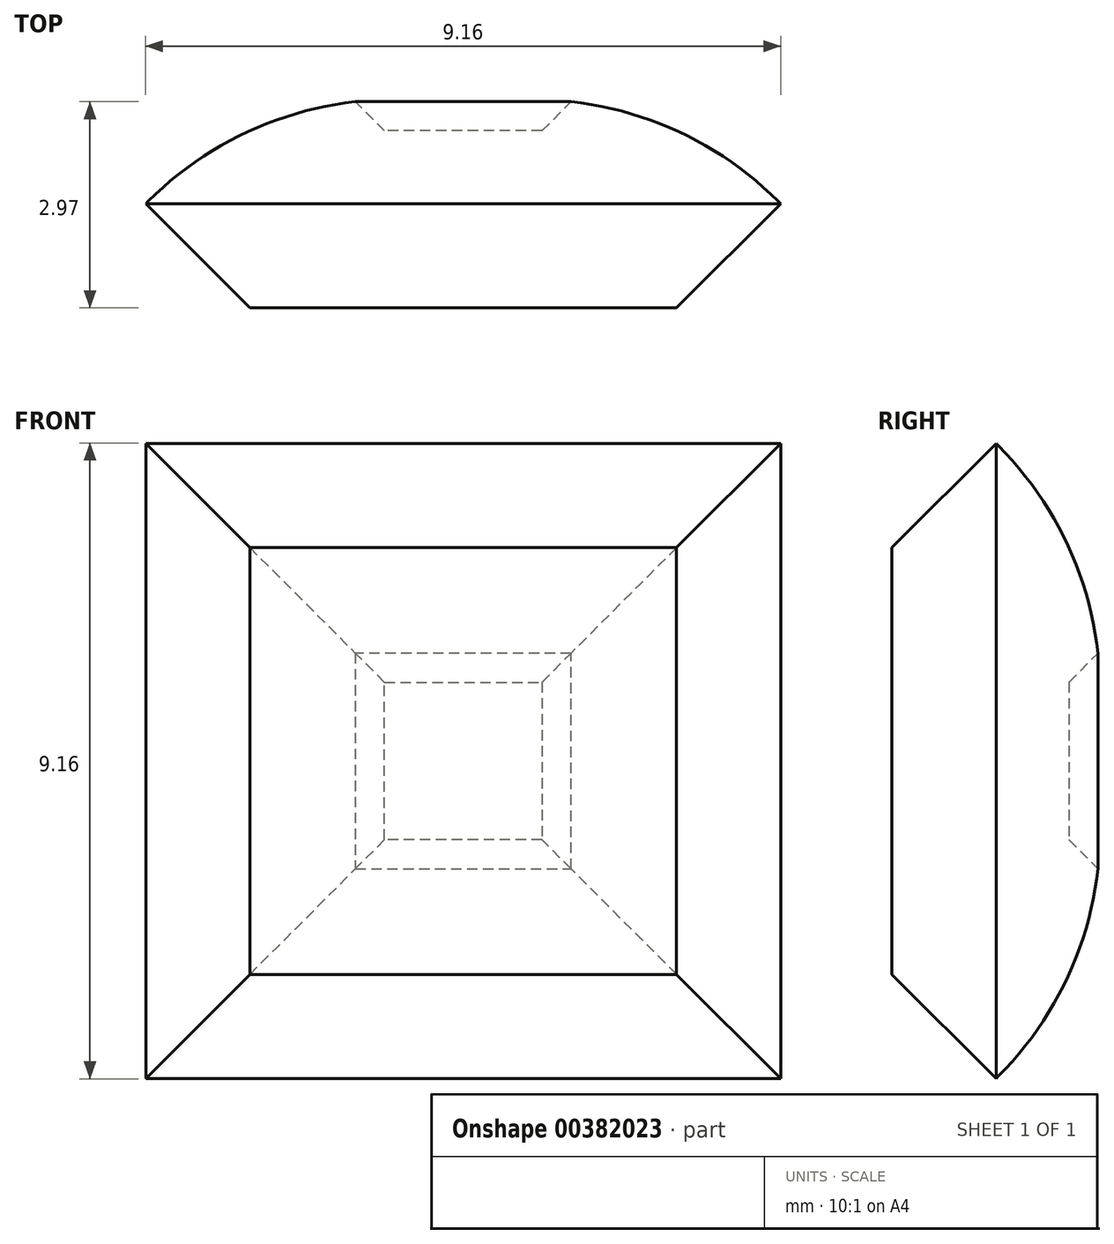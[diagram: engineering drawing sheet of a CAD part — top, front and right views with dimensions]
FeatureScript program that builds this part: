
annotation { "Feature Type Name" : "Feature", "Feature Type Description" : "" }
export const myFeature = defineFeature(function(context is Context, id is Id, definition is map)
    precondition{}
    {
        {
            var Q0;
            Q0=qCreatedBy(makeId("Front.planeOp"),FACE);
            var sketch = newSketch(context, id + "F0", { "sketchPlane" : qUnion([Q0])});
            skLineSegment(sketch, "E0.bottom", {"start": v(0, 0) * mm, "end": v(4.58, 0) * mm});
            skLineSegment(sketch, "E0.top", {"start": v(0, 4.58) * mm, "end": v(4.58, 4.58) * mm});
            skLineSegment(sketch, "E0.right", {"start": v(4.58, 0) * mm, "end": v(4.58, 4.58) * mm});
            skLineSegment(sketch, "E1.MirrorCS", {"start": v(0, 4.58) * mm, "end": v(-4.58, 4.58) * mm});
            skLineSegment(sketch, "E2.MirrorCS", {"start": v(-4.58, 0) * mm, "end": v(-4.58, 4.58) * mm});
            skLineSegment(sketch, "E3.MirrorCS", {"start": v(0, -4.58) * mm, "end": v(-4.58, -4.58) * mm});
            skLineSegment(sketch, "E4.MirrorCS", {"start": v(0, -4.58) * mm, "end": v(4.58, -4.58) * mm});
            skLineSegment(sketch, "E5.MirrorCS", {"start": v(-4.58, 0) * mm, "end": v(-4.58, -4.58) * mm});
            skLineSegment(sketch, "E6.MirrorCS", {"start": v(4.58, 0) * mm, "end": v(4.58, -4.58) * mm});
            skSolve(sketch);
        }
        {
            var Q0;
            Q0 = qSketchRegion(id + "F0", true);
            extrude(context, id + "F1", {"entities" : qUnion([Q0]), "depth" : 3 * mm});
        }
        {
            var Q0;
            Q0=makeQuery(id+"F1.opExtrude","CAP_FACE",FACE,{"disambiguationData":[OSD([sQuery(id+"F0.wireOp",EDGE,"E0.top"),sQuery(id+"F0.wireOp",EDGE,"E0.right"),sQuery(id+"F0.wireOp",EDGE,"E1.MirrorCS"),sQuery(id+"F0.wireOp",EDGE,"E2.MirrorCS"),sQuery(id+"F0.wireOp",EDGE,"E3.MirrorCS"),sQuery(id+"F0.wireOp",EDGE,"E4.MirrorCS"),sQuery(id+"F0.wireOp",EDGE,"E5.MirrorCS"),sQuery(id+"F0.wireOp",EDGE,"E6.MirrorCS")])],"isStart":false});
            var Q1;
            Q1=makeQuery(id+"F1.opExtrude","CAP_FACE",FACE,{"disambiguationData":[OSD([sQuery(id+"F0.wireOp",EDGE,"E0.top"),sQuery(id+"F0.wireOp",EDGE,"E0.right"),sQuery(id+"F0.wireOp",EDGE,"E1.MirrorCS"),sQuery(id+"F0.wireOp",EDGE,"E2.MirrorCS"),sQuery(id+"F0.wireOp",EDGE,"E3.MirrorCS"),sQuery(id+"F0.wireOp",EDGE,"E4.MirrorCS"),sQuery(id+"F0.wireOp",EDGE,"E5.MirrorCS"),sQuery(id+"F0.wireOp",EDGE,"E6.MirrorCS")])],"isStart":true});
            chamfer(context, id + "F2", {"entities" : qUnion([Q0, Q1]), "chamferType" : ChamferType.OFFSET_ANGLE, "width" : 1.5 * mm, "oppositeDirection" : false, "angle" : 45 * degree, "tangentPropagation" : true});
        }
        {
            var Q0;
            Q0=makeQuery(id+"F1.opExtrude","CAP_FACE",FACE,{"disambiguationData":[OSD([sQuery(id+"F0.wireOp",EDGE,"E0.top"),sQuery(id+"F0.wireOp",EDGE,"E0.right"),sQuery(id+"F0.wireOp",EDGE,"E1.MirrorCS"),sQuery(id+"F0.wireOp",EDGE,"E2.MirrorCS"),sQuery(id+"F0.wireOp",EDGE,"E3.MirrorCS"),sQuery(id+"F0.wireOp",EDGE,"E4.MirrorCS"),sQuery(id+"F0.wireOp",EDGE,"E5.MirrorCS"),sQuery(id+"F0.wireOp",EDGE,"E6.MirrorCS")])],"isStart":true});
            var sketch = newSketch(context, id + "F3", { "sketchPlane" : qUnion([Q0])});
            skLineSegment(sketch, "E7.bottom", {"start": v(0, 0) * mm, "end": v(-1.74, 0) * mm});
            skLineSegment(sketch, "E7.top", {"start": v(0, 1.74) * mm, "end": v(-1.74, 1.74) * mm});
            skLineSegment(sketch, "E7.left", {"start": v(0, 0) * mm, "end": v(0, 1.74) * mm});
            skLineSegment(sketch, "E7.right", {"start": v(-1.74, 0) * mm, "end": v(-1.74, 1.74) * mm});
            skLineSegment(sketch, "E8.MirrorCS", {"start": v(0, 1.74) * mm, "end": v(1.74, 1.74) * mm});
            skLineSegment(sketch, "E9.MirrorCS", {"start": v(1.74, 0) * mm, "end": v(1.74, 1.74) * mm});
            skLineSegment(sketch, "E10.MirrorCS", {"start": v(0, -1.74) * mm, "end": v(1.74, -1.74) * mm});
            skLineSegment(sketch, "E11.MirrorCS", {"start": v(0, -1.74) * mm, "end": v(-1.74, -1.74) * mm});
            skLineSegment(sketch, "E12.MirrorCS", {"start": v(-1.74, 0) * mm, "end": v(-1.74, -1.74) * mm});
            skLineSegment(sketch, "E13.MirrorCS", {"start": v(1.74, 0) * mm, "end": v(1.74, -1.74) * mm});
            skSolve(sketch);
        }
        {
            var Q0;
            Q0 = qSketchRegion(id + "F3", true);
            extrude(context, id + "F4", {"entities" : qUnion([Q0]), "operationType" : NewBodyOperationType.REMOVE, "oppositeDirection" : true, "depth" : 0.45 * mm});
        }
        {
            var Q0;
            Q0=makeQuery(id+"F4.boolean.opBoolean","COPY",FACE,{"derivedFrom":makeQuery(id+"F4.opExtrude","CAP_FACE",FACE,{"disambiguationData":[OSD([sQuery(id+"F3.wireOp",EDGE,"E7.top"),sQuery(id+"F3.wireOp",EDGE,"E7.right"),sQuery(id+"F3.wireOp",EDGE,"E8.MirrorCS"),sQuery(id+"F3.wireOp",EDGE,"E9.MirrorCS"),sQuery(id+"F3.wireOp",EDGE,"E10.MirrorCS"),sQuery(id+"F3.wireOp",EDGE,"E11.MirrorCS"),sQuery(id+"F3.wireOp",EDGE,"E12.MirrorCS"),sQuery(id+"F3.wireOp",EDGE,"E13.MirrorCS")])],"isStart":false})});
            chamfer(context, id + "F5", {"entities" : qUnion([Q0]), "width" : 0.6 * mm, "tangentPropagation" : true});
        }
        {
            var Q0;
            {var subQ0=sQuery(id+"F0.wireOp",EDGE,"E6.MirrorCS");var subQ1=sQuery(id+"F0.wireOp",EDGE,"E0.right");Q0=makeQuery(id+"F2.opChamfer","BLEND_EDGE",EDGE,{"blendedFrom":[makeQuery(id+"F1.opExtrude","CAP_EDGE",EDGE,{"disambiguationData":[OSD([subQ1,subQ0])],"isStart":true}),makeQuery(id+"F1.opExtrude","CAP_FACE",FACE,{"disambiguationData":[OSD([sQuery(id+"F0.wireOp",EDGE,"E0.top"),subQ1,sQuery(id+"F0.wireOp",EDGE,"E1.MirrorCS"),sQuery(id+"F0.wireOp",EDGE,"E2.MirrorCS"),sQuery(id+"F0.wireOp",EDGE,"E3.MirrorCS"),sQuery(id+"F0.wireOp",EDGE,"E4.MirrorCS"),sQuery(id+"F0.wireOp",EDGE,"E5.MirrorCS"),subQ0])],"isStart":true})],"blendedInto":[makeQuery(id+"F1.opExtrude","CAP_FACE",FACE,{"disambiguationData":[OSD([sQuery(id+"F0.wireOp",EDGE,"E0.top"),subQ1,sQuery(id+"F0.wireOp",EDGE,"E1.MirrorCS"),sQuery(id+"F0.wireOp",EDGE,"E2.MirrorCS"),sQuery(id+"F0.wireOp",EDGE,"E3.MirrorCS"),sQuery(id+"F0.wireOp",EDGE,"E4.MirrorCS"),sQuery(id+"F0.wireOp",EDGE,"E5.MirrorCS"),subQ0])],"isStart":true})]});}
            var Q1;
            {var subQ0=sQuery(id+"F0.wireOp",EDGE,"E1.MirrorCS");var subQ1=sQuery(id+"F0.wireOp",EDGE,"E0.top");Q1=makeQuery(id+"F2.opChamfer","BLEND_EDGE",EDGE,{"blendedFrom":[makeQuery(id+"F1.opExtrude","CAP_EDGE",EDGE,{"disambiguationData":[OSD([subQ1,subQ0])],"isStart":true}),makeQuery(id+"F1.opExtrude","CAP_FACE",FACE,{"disambiguationData":[OSD([subQ1,sQuery(id+"F0.wireOp",EDGE,"E0.right"),subQ0,sQuery(id+"F0.wireOp",EDGE,"E2.MirrorCS"),sQuery(id+"F0.wireOp",EDGE,"E3.MirrorCS"),sQuery(id+"F0.wireOp",EDGE,"E4.MirrorCS"),sQuery(id+"F0.wireOp",EDGE,"E5.MirrorCS"),sQuery(id+"F0.wireOp",EDGE,"E6.MirrorCS")])],"isStart":true})],"blendedInto":[makeQuery(id+"F1.opExtrude","CAP_FACE",FACE,{"disambiguationData":[OSD([subQ1,sQuery(id+"F0.wireOp",EDGE,"E0.right"),subQ0,sQuery(id+"F0.wireOp",EDGE,"E2.MirrorCS"),sQuery(id+"F0.wireOp",EDGE,"E3.MirrorCS"),sQuery(id+"F0.wireOp",EDGE,"E4.MirrorCS"),sQuery(id+"F0.wireOp",EDGE,"E5.MirrorCS"),sQuery(id+"F0.wireOp",EDGE,"E6.MirrorCS")])],"isStart":true})]});}
            var Q2;
            {var subQ0=sQuery(id+"F0.wireOp",EDGE,"E5.MirrorCS");var subQ1=sQuery(id+"F0.wireOp",EDGE,"E2.MirrorCS");Q2=makeQuery(id+"F2.opChamfer","BLEND_EDGE",EDGE,{"blendedFrom":[makeQuery(id+"F1.opExtrude","CAP_EDGE",EDGE,{"disambiguationData":[OSD([subQ1,subQ0])],"isStart":true}),makeQuery(id+"F1.opExtrude","CAP_FACE",FACE,{"disambiguationData":[OSD([sQuery(id+"F0.wireOp",EDGE,"E0.top"),sQuery(id+"F0.wireOp",EDGE,"E0.right"),sQuery(id+"F0.wireOp",EDGE,"E1.MirrorCS"),subQ1,sQuery(id+"F0.wireOp",EDGE,"E3.MirrorCS"),sQuery(id+"F0.wireOp",EDGE,"E4.MirrorCS"),subQ0,sQuery(id+"F0.wireOp",EDGE,"E6.MirrorCS")])],"isStart":true})],"blendedInto":[makeQuery(id+"F1.opExtrude","CAP_FACE",FACE,{"disambiguationData":[OSD([sQuery(id+"F0.wireOp",EDGE,"E0.top"),sQuery(id+"F0.wireOp",EDGE,"E0.right"),sQuery(id+"F0.wireOp",EDGE,"E1.MirrorCS"),subQ1,sQuery(id+"F0.wireOp",EDGE,"E3.MirrorCS"),sQuery(id+"F0.wireOp",EDGE,"E4.MirrorCS"),subQ0,sQuery(id+"F0.wireOp",EDGE,"E6.MirrorCS")])],"isStart":true})]});}
            var Q3;
            {var subQ0=sQuery(id+"F0.wireOp",EDGE,"E4.MirrorCS");var subQ1=sQuery(id+"F0.wireOp",EDGE,"E3.MirrorCS");Q3=makeQuery(id+"F2.opChamfer","BLEND_EDGE",EDGE,{"blendedFrom":[makeQuery(id+"F1.opExtrude","CAP_EDGE",EDGE,{"disambiguationData":[OSD([subQ1,subQ0])],"isStart":true}),makeQuery(id+"F1.opExtrude","CAP_FACE",FACE,{"disambiguationData":[OSD([sQuery(id+"F0.wireOp",EDGE,"E0.top"),sQuery(id+"F0.wireOp",EDGE,"E0.right"),sQuery(id+"F0.wireOp",EDGE,"E1.MirrorCS"),sQuery(id+"F0.wireOp",EDGE,"E2.MirrorCS"),subQ1,subQ0,sQuery(id+"F0.wireOp",EDGE,"E5.MirrorCS"),sQuery(id+"F0.wireOp",EDGE,"E6.MirrorCS")])],"isStart":true})],"blendedInto":[makeQuery(id+"F1.opExtrude","CAP_FACE",FACE,{"disambiguationData":[OSD([sQuery(id+"F0.wireOp",EDGE,"E0.top"),sQuery(id+"F0.wireOp",EDGE,"E0.right"),sQuery(id+"F0.wireOp",EDGE,"E1.MirrorCS"),sQuery(id+"F0.wireOp",EDGE,"E2.MirrorCS"),subQ1,subQ0,sQuery(id+"F0.wireOp",EDGE,"E5.MirrorCS"),sQuery(id+"F0.wireOp",EDGE,"E6.MirrorCS")])],"isStart":true})]});}
            fillet(context, id + "F6", {"entities" : qUnion([Q0, Q1, Q2, Q3]), "radius" : 5 * mm, "tangentPropagation" : true, "allowEdgeOverflow" : false});
        }
    });
